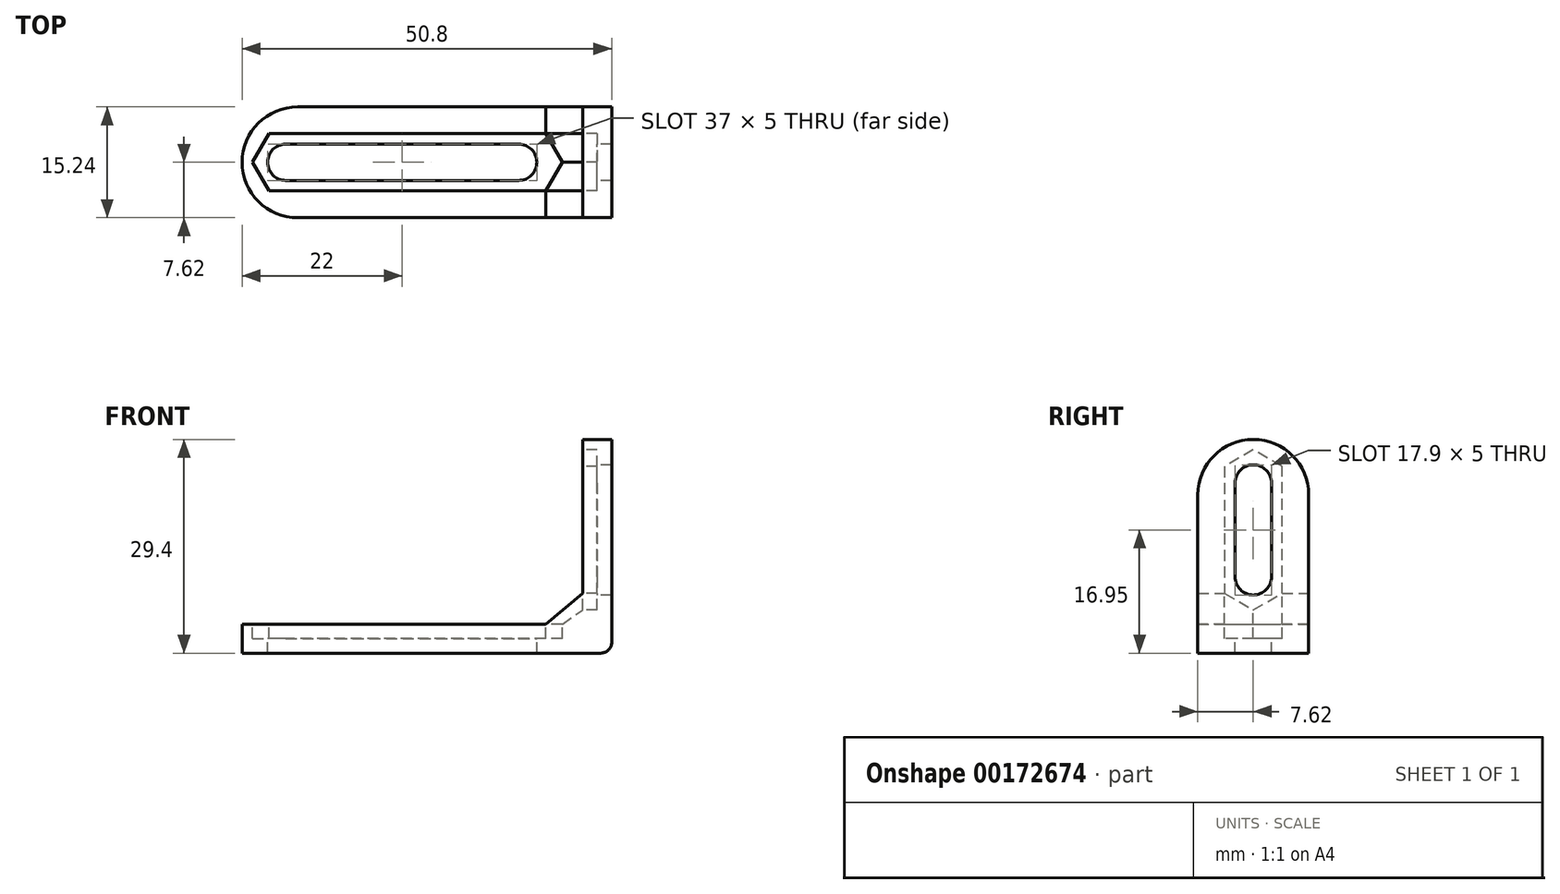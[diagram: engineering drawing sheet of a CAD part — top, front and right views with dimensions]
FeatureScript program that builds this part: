
annotation { "Feature Type Name" : "Feature", "Feature Type Description" : "" }
export const myFeature = defineFeature(function(context is Context, id is Id, definition is map)
    precondition{}
    {
        {
            var Q0;
            Q0=qCreatedBy(makeId("Front.planeOp"),FACE);
            var sketch = newSketch(context, id + "F0", { "sketchPlane" : qUnion([Q0])});
            skLineSegment(sketch, "E0.top", {"start": v(-4, 3) * mm, "end": v(-50.8, 3) * mm});
            skLineSegment(sketch, "E1.top", {"start": v(-1.5, 28.4) * mm, "end": v(-1.5, 28.4) * mm});
            skLineSegment(sketch, "E1.left", {"start": v(0, 0.5) * mm, "end": v(0, 28.4) * mm});
            skLineSegment(sketch, "E1.right", {"start": v(-4, 3) * mm, "end": v(-4, 28.4) * mm});
            skPoint(sketch, "E2.visualSharp", {"position": v(-4, 3) * mm});
            skPoint(sketch, "E3.visualSharp", {"position": v(0, 0) * mm});
            skPoint(sketch, "E4.visualSharp", {"position": v(-4, 28.4) * mm});
            skPoint(sketch, "E5.visualSharp", {"position": v(0, 28.4) * mm});
            skPoint(sketch, "E6.visualSharp", {"position": v(-53.3, 3) * mm});
            skLineSegment(sketch, "E7", {"start": v(-50.8, -1) * mm, "end": v(-1.5, -1) * mm});
            skPoint(sketch, "E8.visualSharp", {"position": v(-53.3, -1) * mm});
            skPoint(sketch, "E9.visualSharp", {"position": v(0, -1) * mm});
            skArc(sketch, "E9.filletArc", {"start": v(-1.5, -1) * mm, "mid": v(-0.44, -0.56) * mm, "end": v(0, 0.5) * mm});
            skLineSegment(sketch, "E10", {"start": v(-4, 28.4) * mm, "end": v(0, 28.4) * mm});
            skLineSegment(sketch, "E11.trimOffspring", {"start": v(-50.8, 3) * mm, "end": v(-50.8, -1) * mm});
            skSolve(sketch);
        }
        {
            var Q0;
            Q0 = qSketchRegion(id + "F0", true);
            extrude(context, id + "F1", {"entities" : qUnion([Q0]), "depth" : 15.24 * mm});
        }
        {
            var Q0;
            Q0=makeQuery(id+"F1.opExtrude","SWEPT_FACE",FACE,{"disambiguationData":[OSD([sQuery(id+"F0.wireOp",EDGE,"E1.right")])]});
            var sketch = newSketch(context, id + "F2", { "sketchPlane" : qUnion([Q0])});
            skLineSegment(sketch, "E12", {"start": v(7.62, 22.4) * mm, "end": v(7.62, 9.5) * mm});
            skArc(sketch, "E13.0.startCap", {"start": v(5.12, 22.4) * mm, "mid": v(7.62, 24.9) * mm, "end": v(10.12, 22.4) * mm});
            skArc(sketch, "E13.0.endCap", {"start": v(10.12, 9.5) * mm, "mid": v(7.62, 7) * mm, "end": v(5.12, 9.5) * mm});
            skLineSegment(sketch, "E13.0.left", {"start": v(10.12, 22.4) * mm, "end": v(10.12, 9.5) * mm});
            skLineSegment(sketch, "E13.0.right", {"start": v(5.12, 22.4) * mm, "end": v(5.12, 9.5) * mm});
            skLineSegment(sketch, "E14.0.left", {"start": v(11.57, 22.4) * mm, "end": v(11.57, 9.5) * mm});
            skLineSegment(sketch, "E14.0.right", {"start": v(3.67, 22.4) * mm, "end": v(3.67, 9.5) * mm});
            skArc(sketch, "E15.cCircle", {"start": v(3.67, 22.4) * mm, "mid": v(7.62, 18.45) * mm, "end": v(11.57, 22.4) * mm, "construction": true});
            skLineSegment(sketch, "E15.0", {"start": v(11.57, 24.68) * mm, "end": v(11.57, 20.12) * mm});
            skLineSegment(sketch, "E15.3", {"start": v(3.67, 20.12) * mm, "end": v(3.67, 24.68) * mm});
            skLineSegment(sketch, "E15.4", {"start": v(3.67, 24.68) * mm, "end": v(7.62, 26.96) * mm});
            skLineSegment(sketch, "E15.5", {"start": v(7.62, 26.96) * mm, "end": v(11.57, 24.68) * mm});
            skPoint(sketch, "E15.0.midPoint", {"position": v(11.57, 22.4) * mm});
            skArc(sketch, "E16.cCircle", {"start": v(11.57, 9.5) * mm, "mid": v(7.62, 13.45) * mm, "end": v(3.67, 9.5) * mm, "construction": true});
            skLineSegment(sketch, "E16.0", {"start": v(11.57, 11.78) * mm, "end": v(11.57, 7.22) * mm});
            skLineSegment(sketch, "E16.1", {"start": v(11.57, 7.22) * mm, "end": v(7.62, 4.94) * mm});
            skLineSegment(sketch, "E16.2", {"start": v(7.62, 4.94) * mm, "end": v(3.67, 7.22) * mm});
            skLineSegment(sketch, "E16.3", {"start": v(3.67, 7.22) * mm, "end": v(3.67, 11.78) * mm});
            skPoint(sketch, "E16.0.midPoint", {"position": v(11.57, 9.5) * mm});
            skPoint(sketch, "E17.orphan", {"position": v(7.62, 14.06) * mm});
            skSolve(sketch);
        }
        {
            var Q0;
            Q0 = qSketchRegion(id + "F2", true);
            extrude(context, id + "F3", {"entities" : qUnion([Q0]), "operationType" : NewBodyOperationType.REMOVE, "oppositeDirection" : true, "depth" : 2 * mm});
        }
        {
            var Q0;
            Q0=makeQuery(id+"F3.boolean.opBoolean","SPLIT",FACE,{"disambiguationData":[TD([makeQuery(id+"F3.opExtrude","SWEPT_FACE",FACE,{"disambiguationData":[OSD([sQuery(id+"F2.wireOp",EDGE,"E13.0.startCap")])]})])],"derivedFrom":makeQuery(id+"F1.opExtrude","SWEPT_FACE",FACE,{"disambiguationData":[OSD([sQuery(id+"F0.wireOp",EDGE,"E1.right")])]})});
            extrude(context, id + "F4", {"entities" : qUnion([Q0]), "operationType" : NewBodyOperationType.REMOVE, "endBound" : BoundingType.UP_TO_NEXT, "oppositeDirection" : true, "depth" : 25.4 * mm});
        }
        {
            var Q0;
            Q0=makeQuery(id+"F1.opExtrude","SWEPT_FACE",FACE,{"disambiguationData":[OSD([sQuery(id+"F0.wireOp",EDGE,"E0.top")])]});
            var sketch = newSketch(context, id + "F5", { "sketchPlane" : qUnion([Q0])});
            skLineSegment(sketch, "E18", {"start": v(-44.8, -7.62) * mm, "end": v(-12.8, -7.62) * mm});
            skPoint(sketch, "E18.startSnap0", {"position": v(-4, -7.62) * mm});
            skPoint(sketch, "E18.endSnap0", {"position": v(-6.8, -7.62) * mm});
            skArc(sketch, "E19.0.startCap", {"start": v(-44.8, -10.12) * mm, "mid": v(-47.3, -7.62) * mm, "end": v(-44.8, -5.12) * mm});
            skArc(sketch, "E19.0.endCap", {"start": v(-12.8, -5.12) * mm, "mid": v(-10.3, -7.62) * mm, "end": v(-12.8, -10.12) * mm});
            skLineSegment(sketch, "E19.0.left", {"start": v(-44.8, -5.12) * mm, "end": v(-12.8, -5.12) * mm});
            skLineSegment(sketch, "E19.0.right", {"start": v(-44.8, -10.12) * mm, "end": v(-12.8, -10.12) * mm});
            skArc(sketch, "E20.cCircle", {"start": v(-44.8, -11.57) * mm, "mid": v(-40.85, -7.62) * mm, "end": v(-44.8, -3.67) * mm, "construction": true});
            skLineSegment(sketch, "E20.0", {"start": v(-9.08, -11.57) * mm, "end": v(-47.08, -11.57) * mm});
            skLineSegment(sketch, "E20.1", {"start": v(-47.08, -11.57) * mm, "end": v(-49.36, -7.62) * mm});
            skLineSegment(sketch, "E20.2", {"start": v(-49.36, -7.62) * mm, "end": v(-47.08, -3.67) * mm});
            skLineSegment(sketch, "E20.3", {"start": v(-47.08, -3.67) * mm, "end": v(-9.08, -3.67) * mm});
            skPoint(sketch, "E20.0.midPoint", {"position": v(-44.8, -11.57) * mm});
            skLineSegment(sketch, "E21.4", {"start": v(-9.08, -3.67) * mm, "end": v(-6.8, -7.62) * mm});
            skLineSegment(sketch, "E21.5", {"start": v(-6.8, -7.62) * mm, "end": v(-9.08, -11.57) * mm});
            skPoint(sketch, "E22.orphan", {"position": v(-40.24, -7.62) * mm});
            skSolve(sketch);
        }
        {
            var Q0;
            Q0 = qSketchRegion(id + "F5", true);
            extrude(context, id + "F6", {"entities" : qUnion([Q0]), "operationType" : NewBodyOperationType.REMOVE, "oppositeDirection" : true, "depth" : 2 * mm});
        }
        {
            var Q0;
            Q0=makeQuery(id+"F6.boolean.opBoolean","SPLIT",FACE,{"disambiguationData":[TD([makeQuery(id+"F6.opExtrude","SWEPT_FACE",FACE,{"disambiguationData":[OSD([sQuery(id+"F5.wireOp",EDGE,"E19.0.startCap")])]})])],"derivedFrom":makeQuery(id+"F1.opExtrude","SWEPT_FACE",FACE,{"disambiguationData":[OSD([sQuery(id+"F0.wireOp",EDGE,"E0.top")])]})});
            extrude(context, id + "F7", {"entities" : qUnion([Q0]), "operationType" : NewBodyOperationType.REMOVE, "endBound" : BoundingType.UP_TO_NEXT, "oppositeDirection" : true, "depth" : 25.4 * mm});
        }
        {
            var Q0;
            Q0=makeQuery(id+"F1.opExtrude","CAP_EDGE",EDGE,{"disambiguationData":[OSD([sQuery(id+"F0.wireOp",EDGE,"E11.trimOffspring")])],"isStart":false});
            var Q1;
            Q1=makeQuery(id+"F1.opExtrude","CAP_EDGE",EDGE,{"disambiguationData":[OSD([sQuery(id+"F0.wireOp",EDGE,"E11.trimOffspring")])],"isStart":true});
            fillet(context, id + "F8", {"entities" : qUnion([Q0, Q1]), "radius" : 7.62 * mm, "tangentPropagation" : true, "allowEdgeOverflow" : false});
        }
        {
            var Q0;
            {var subQ0=sQuery(id+"F0.wireOp",EDGE,"E1.right");var subQ6=sQuery(id+"F0.wireOp",EDGE,"E0.top");Q0=makeQuery(id+"F6.boolean.opBoolean","SPLIT",FACE,{"disambiguationData":[TD([makeQuery(id+"F1.opExtrude","SWEPT_FACE",FACE,{"disambiguationData":[OSD([subQ0])]})])],"derivedFrom":makeQuery(id+"F1.opExtrude","SWEPT_FACE",FACE,{"disambiguationData":[OSD([subQ6])]})});}
            var sketch = newSketch(context, id + "F9", { "sketchPlane" : qUnion([Q0])});
            skLineSegment(sketch, "E23.top", {"start": v(-9.08, -15.24) * mm, "end": v(-4, -15.24) * mm});
            skLineSegment(sketch, "E23.left", {"start": v(-9.08, 0) * mm, "end": v(-9.08, -15.24) * mm});
            skLineSegment(sketch, "E23.right", {"start": v(-4, 0) * mm, "end": v(-4, -15.24) * mm});
            skLineSegment(sketch, "E24.top", {"start": v(-9.08, 0) * mm, "end": v(-4, 0) * mm});
            skSolve(sketch);
        }
        {
            var Q0;
            {var subQ4=sQuery(id+"F0.wireOp",EDGE,"E1.right");var subQ6=sQuery(id+"F0.wireOp",EDGE,"E0.top");Q0=makeQuery(id+"F3.boolean.opBoolean","SPLIT",FACE,{"disambiguationData":[TD([makeQuery(id+"F1.opExtrude","SWEPT_FACE",FACE,{"disambiguationData":[OSD([subQ6])]})])],"derivedFrom":makeQuery(id+"F1.opExtrude","SWEPT_FACE",FACE,{"disambiguationData":[OSD([subQ4])]})});}
            var sketch = newSketch(context, id + "F10", { "sketchPlane" : qUnion([Q0])});
            skLineSegment(sketch, "E25.right", {"start": v(0, 7.22) * mm, "end": v(0, 3) * mm});
            skLineSegment(sketch, "E26.bottom", {"start": v(15.24, 3) * mm, "end": v(0, 3) * mm});
            skLineSegment(sketch, "E26.top", {"start": v(15.24, 7.22) * mm, "end": v(0, 7.22) * mm});
            skLineSegment(sketch, "E26.left", {"start": v(15.24, 3) * mm, "end": v(15.24, 7.22) * mm});
            skSolve(sketch);
        }
        {
            var Q0;
            {var subQ2=sQuery(id+"F9.wireOp",EDGE,"E23.top");Q0=makeQuery(id+"F9.imprint","IMPRINT",FACE,{"disambiguationData":[TD([[makeQuery(id+"F9.imprint","IMPRINT",EDGE,{"derivedFrom":subQ2}),-1.0]])]});}
            var Q1;
            {var subQ5=sQuery(id+"F10.wireOp",EDGE,"E25.right");Q1=makeQuery(id+"F10.imprint","IMPRINT",FACE,{"disambiguationData":[TD([[makeQuery(id+"F10.imprint","IMPRINT",EDGE,{"derivedFrom":subQ5}),-1.0]])]});}
            var Q2;
            Q2=makeQuery(id+"F9.imprint","IMPRINT",FACE,{"disambiguationData":[TD([[makeQuery(id+"F9.imprint","IMPRINT",EDGE,{"derivedFrom":sQuery(id+"F9.wireOp",EDGE,"bt2bfATN-E2v8-TheF-lZmc-CfuJhGe66lLX.bottom")}),1.0]])]});
            var Q3;
            Q3=makeQuery(id+"F10.imprint","IMPRINT",FACE,{"disambiguationData":[TD([[makeQuery(id+"F10.imprint","IMPRINT",EDGE,{"derivedFrom":sQuery(id+"F10.wireOp",EDGE,"E25.bottom")}),1.0]])]});
            var Q4;
            Q4=sQuery(id+"F9.wireOp",VERTEX,"E23.top.start");
            var Q5;
            Q5=sQuery(id+"F10.wireOp",VERTEX,"E26.left.end");
            loft(context, id + "F11", {"operationType" : NewBodyOperationType.ADD, "sheetProfilesArray" : [{ "sheetProfileEntities" : qUnion([Q0]) }, { "sheetProfileEntities" : qUnion([Q1]) }], "wireProfilesArray" : [{ "wireProfileEntities" : qUnion([Q2]) }, { "wireProfileEntities" : qUnion([Q3]) }], "matchConnections" : true, "connections" : [{ "connectionEntities" : qUnion([Q4, Q5]), "connectionEdgeQueries" : qUnion([]), "connectionEdgeParameters" : [] }]});
        }
        {
            var Q0;
            Q0=makeQuery(id+"F1.opExtrude","CAP_EDGE",EDGE,{"disambiguationData":[OSD([sQuery(id+"F0.wireOp",EDGE,"E10")])],"isStart":false});
            var Q1;
            Q1=makeQuery(id+"F1.opExtrude","CAP_EDGE",EDGE,{"disambiguationData":[OSD([sQuery(id+"F0.wireOp",EDGE,"E10")])],"isStart":true});
            fillet(context, id + "F12", {"entities" : qUnion([Q0, Q1]), "radius" : 7.62 * mm, "tangentPropagation" : true, "allowEdgeOverflow" : false});
        }
    });
